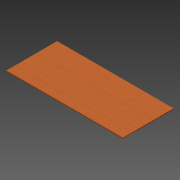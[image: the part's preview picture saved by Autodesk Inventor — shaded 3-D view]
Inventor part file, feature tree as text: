
AUTODESK INVENTOR PART (.ipt)
format: ipt  version: 2013 (Build 170138000, 138)  size: 75,776 bytes
history: native  units: in
note: dims shown in document units (in); Inventor stores cm internally (conversion verified against a paired STEP export)
features: extrude x1, sketch x1
ambient origin geometry x8: Origin, YZ Plane, XZ Plane, XY Plane, X Axis, Y Axis, Z Axis, Center Point
bodies: Solid1 (feature_tree)
feature tree (2):
  extrude  "Extrusion1"  Depth=24.0in
  sketch  "Sketch1"  dims[d0=55.0in d1=24.0in d2=0.5in d3=0.0in]
